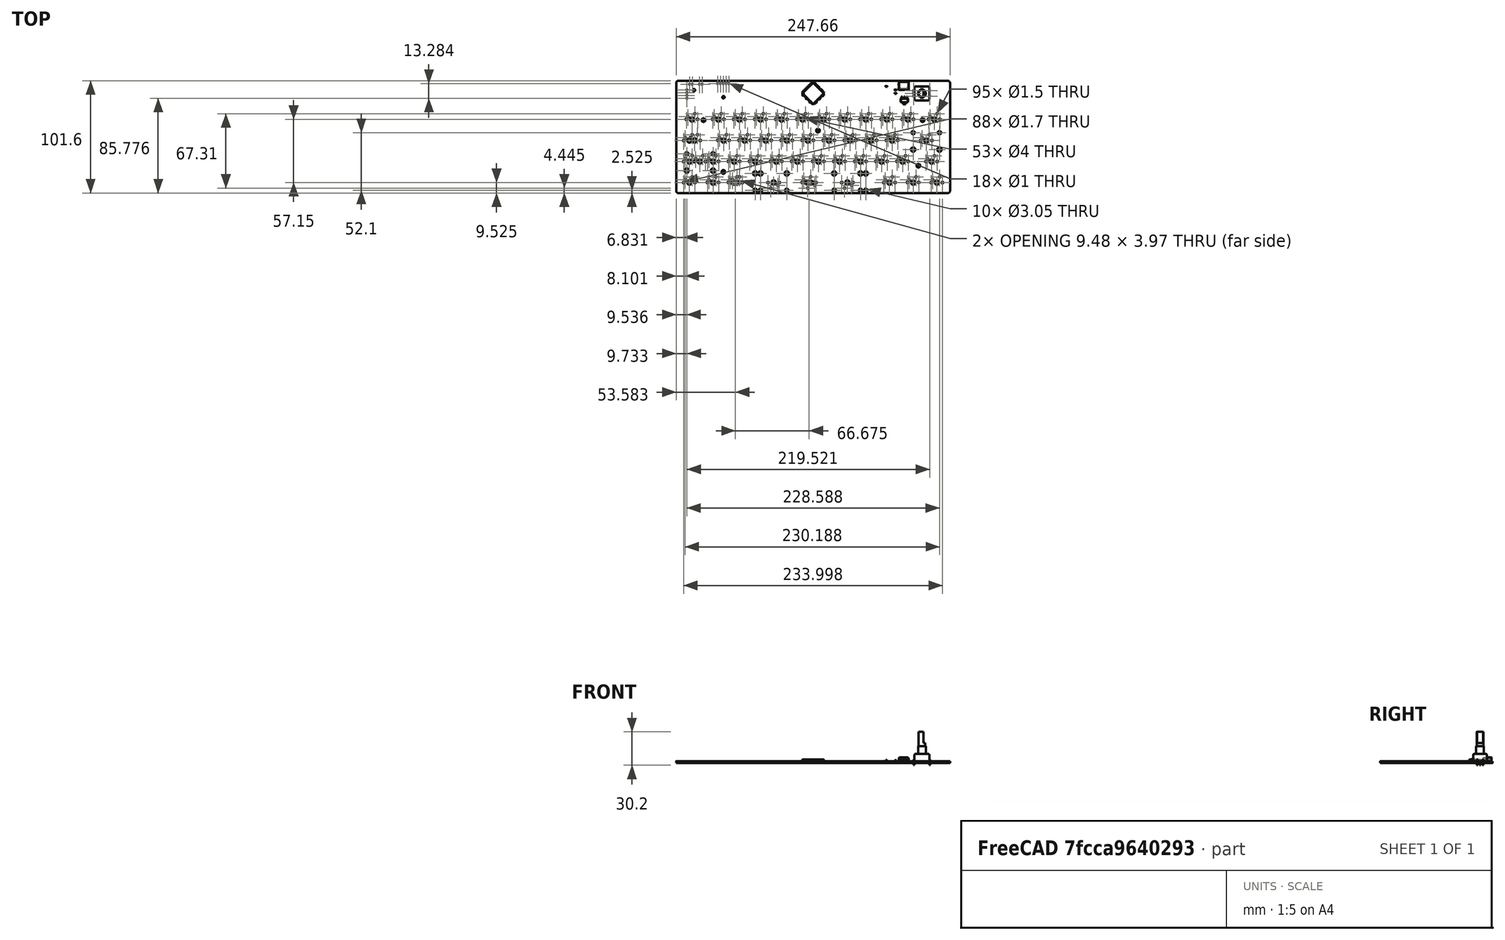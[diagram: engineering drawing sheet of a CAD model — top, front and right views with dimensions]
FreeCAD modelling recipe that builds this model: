
FCSTD DOCUMENT  (FreeCAD 0.19R22756 (Git))
Label: R79_SquashPCB
License: All rights reserved
LicenseURL: http://en.wikipedia.org/wiki/All_rights_reserved
objects: App::Link×9, Part::Feature×8, App::Part×5, PartDesign::CoordinateSystem×3, Sketcher::SketchObject×1
note: 12 computed .brp shape members not serialized (recipe doc carries the construction recipe); baked Part::Feature solids carry a one-line shape summary decoded from their .brp

FEATURE [PartDesign::CoordinateSystem] Local_CS_de64
  AttacherType = Attacher::AttachEngine3D
FEATURE [Part::Feature] Pcb_de64
  Placement = pos=(-123.825,50.8,0) rot=(0,0,1;0rad)
  shape: bbox 247.7 x 101.6 x 1.6 mm, 380 faces (baked)
FEATURE [Sketcher::SketchObject] PCB_Sketch_de64
  sketch-geometry (8):
    g0: LineSegment StartX=-121.92 StartY=50.8 StartZ=0 EndX=121.92 EndY=50.8 EndZ=0
    g1: LineSegment StartX=-123.825 StartY=-48.895 StartZ=0 EndX=-123.825 EndY=48.895 EndZ=0
    g2: LineSegment StartX=121.92 StartY=-50.8 StartZ=0 EndX=-121.92 EndY=-50.8 EndZ=0
    g3: LineSegment StartX=123.825 StartY=48.895 StartZ=0 EndX=123.825 EndY=-48.895 EndZ=0
    g4: ArcOfCircle CenterX=121.92 CenterY=48.895 CenterZ=0 NormalX=0 NormalY=0 NormalZ=1 AngleXU=0 Radius=1.905 StartAngle=0 EndAngle=1.5708
    g5: ArcOfCircle CenterX=121.92 CenterY=-48.895 CenterZ=0 NormalX=0 NormalY=0 NormalZ=1 AngleXU=0 Radius=1.905 StartAngle=4.71239 EndAngle=6.28319
    g6: ArcOfCircle CenterX=-121.92 CenterY=-48.895 CenterZ=0 NormalX=0 NormalY=0 NormalZ=1 AngleXU=0 Radius=1.905 StartAngle=3.14159 EndAngle=4.71239
    g7: ArcOfCircle CenterX=-121.92 CenterY=48.895 CenterZ=0 NormalX=0 NormalY=0 NormalZ=1 AngleXU=0 Radius=1.905 StartAngle=1.5708 EndAngle=3.14159
FEATURE [App::Part] Board_Geoms_de64
  Group = -> [Local_CS_de64,Pcb_de64,PCB_Sketch_de64]
  Origin = -> Origin
FEATURE [Part::Feature] Shape  label="ROT_ENC1_PEC11R-4220K-S0024_5F30CEA1"
  Placement = pos=(90.9244,41.8694,0) rot=(0,0,1;0rad)
  shape: bbox 15 x 12.5 x 30.2 mm, 54 faces (baked)
FEATURE [Part::Feature] Shape002  label="U2_SOT_223_5F285D89"
  Placement = pos=(82.55,32.995,0) rot=(0,0,-1;1.5708rad)
  shape: bbox 6.5 x 7 x 1.7 mm, 78 faces (baked)
FEATURE [Part::Feature] Shape005  label="USBC1_U262-161N-4BVC11_5F1FC831"
  Placement = pos=(81.915,42.53,0) rot=(0,0,1;3.14159rad)
  shape: bbox 8.94 x 7.3 x 3.26 mm, 28 faces (baked)
FEATURE [Part::Feature] Shape006  label="C1_C_0603_1608Metric_5F1FC55F"
  Placement = pos=(74.4475,39.37,0) rot=(0,0,1;3.14159rad)
  shape: bbox 1.6 x 0.8 x 0.8 mm, 28 faces (baked)
FEATURE [App::Link] C1_C_0603_1608Metric_5F1FC55F_ln_  label="C2_C_0603_1608Metric_5F1FC570"
  LinkPlacement = pos=(74.7775,33.02,0) rot=(0,0,1;3.14159rad)
  LinkedObject = -> Shape006
  Placement = pos=(74.7775,33.02,0) rot=(0,0,1;3.14159rad)
FEATURE [Part::Feature] Shape007  label="D1_LED_0603_1608Metric_5F30C0E4"
  Placement = pos=(66.1925,45.72,0) rot=(0,0,1;3.14159rad)
  shape: bbox 1.6 x 0.8 x 1.1 mm, 50 faces (baked)
FEATURE [App::Link] D1_LED_0603_1608Metric_5F30C0E4_ln_  label="D2_LED_0603_1608Metric_5F30D3A8"
  LinkPlacement = pos=(66.1925,39.37,0) rot=(0,0,1;3.14159rad)
  LinkedObject = -> Shape007
  Placement = pos=(66.1925,39.37,0) rot=(0,0,1;3.14159rad)
FEATURE [App::Link] D1_LED_0603_1608Metric_5F30C0E4_ln_001  label="D3_LED_0603_1608Metric_5F30C10A"
  LinkPlacement = pos=(66.1925,33.02,0) rot=(0,0,1;3.14159rad)
  LinkedObject = -> Shape007
  Placement = pos=(66.1925,33.02,0) rot=(0,0,1;3.14159rad)
FEATURE [Part::Feature] Shape008  label="R1_R_0603_1608Metric_5F30E40D"
  Placement = pos=(74.4475,42.545,0) rot=(0,0,1;0rad)
  shape: bbox 1.6 x 0.8 x 0.45 mm, 26 faces (baked)
FEATURE [App::Link] R1_R_0603_1608Metric_5F30E40D_ln_  label="R2_R_0603_1608Metric_5F30DC4E"
  LinkPlacement = pos=(74.4475,45.72,0) rot=(0,0,1;0rad)
  LinkedObject = -> Shape008
  Placement = pos=(74.4475,45.72,0) rot=(0,0,1;0rad)
FEATURE [App::Link] R1_R_0603_1608Metric_5F30E40D_ln_001  label="R3_R_0603_1608Metric_5F1FC6F5"
  LinkPlacement = pos=(-93.98,47.625,0) rot=(0,0,1;3.14159rad)
  LinkedObject = -> Shape008
  Placement = pos=(-93.98,47.625,0) rot=(0,0,1;3.14159rad)
FEATURE [App::Link] R1_R_0603_1608Metric_5F30E40D_ln_002  label="R4_R_0603_1608Metric_5F1FC706"
  LinkPlacement = pos=(-117.258,47.625,0) rot=(0,0,1;3.14159rad)
  LinkedObject = -> Shape008
  Placement = pos=(-117.258,47.625,0) rot=(0,0,1;3.14159rad)
FEATURE [App::Link] R1_R_0603_1608Metric_5F30E40D_ln_003  label="R5_R_0603_1608Metric_5F30D0E7"
  LinkPlacement = pos=(70.6375,45.72,0) rot=(0,0,1;3.14159rad)
  LinkedObject = -> Shape008
  Placement = pos=(70.6375,45.72,0) rot=(0,0,1;3.14159rad)
FEATURE [App::Link] R1_R_0603_1608Metric_5F30E40D_ln_004  label="R6_R_0603_1608Metric_5F30C27F"
  LinkPlacement = pos=(70.6375,39.37,0) rot=(0,0,1;3.14159rad)
  LinkedObject = -> Shape008
  Placement = pos=(70.6375,39.37,0) rot=(0,0,1;3.14159rad)
FEATURE [App::Link] R1_R_0603_1608Metric_5F30E40D_ln_005  label="R7_R_0603_1608Metric_5F30C290"
  LinkPlacement = pos=(70.6375,33.02,0) rot=(0,0,1;3.14159rad)
  LinkedObject = -> Shape008
  Placement = pos=(70.6375,33.02,0) rot=(0,0,1;3.14159rad)
FEATURE [Part::Feature] Shape009  label="U1_LQFP_100_14x14mm_P05mm_5F30CB79"
  Placement = pos=(0,39.37,0) rot=(0,0,1;0.785398rad)
  shape: bbox 19.95 x 19.95 x 1.5 mm, 1544 faces (baked)
FEATURE [App::Part] Top_de64
  Group = -> [Shape,Shape002,Shape005,Shape006,C1_C_0603_1608Metric_5F1FC55F_ln_,Shape007,D1_LED_0603_1608Metric_5F30C0E4_ln_,D1_LED_0603_1608Metric_5F30C0E4_ln_001,Shape008,R1_R_0603_1608Metric_5F30E40D_ln_,R1_R_0603_1608Metric_5F30E40D_ln_001,R1_R_0603_1608Metric_5F30E40D_ln_002,R1_R_0603_1608Metric_5F30E40D_ln_003,R1_R_0603_1608Metric_5F30E40D_ln_004,R1_R_0603_1608Metric_5F30E40D_ln_005,Shape009]
  Origin = -> Origin003
FEATURE [App::Part] Step_Models_de64
  Group = -> [Top_de64]
  Origin = -> Origin002
FEATURE [App::Part] Board_de64  label="squash"
  Group = -> [Board_Geoms_de64,Step_Models_de64]
  Origin = -> Origin001
FEATURE [PartDesign::CoordinateSystem] LCS_0
  AttacherType = Attacher::AttachEngine3D
  MapMode = 2
  Support = -> [X_Axis004]
FEATURE [PartDesign::CoordinateSystem] OLEDPin
  AttacherType = Attacher::AttachEngine3D
  AttachmentOffset = pos=(0,0,0) rot=(0,0,-1;1.5708rad)
  MapMode = 11
  Placement = pos=(-114.097,42.5958,0) rot=(0,0,1;0rad)
  Support = -> [Pcb_de64]
FEATURE [App::Part] Part
  Group = -> [LCS_0,Board_de64,OLEDPin]
  Origin = -> Origin004
